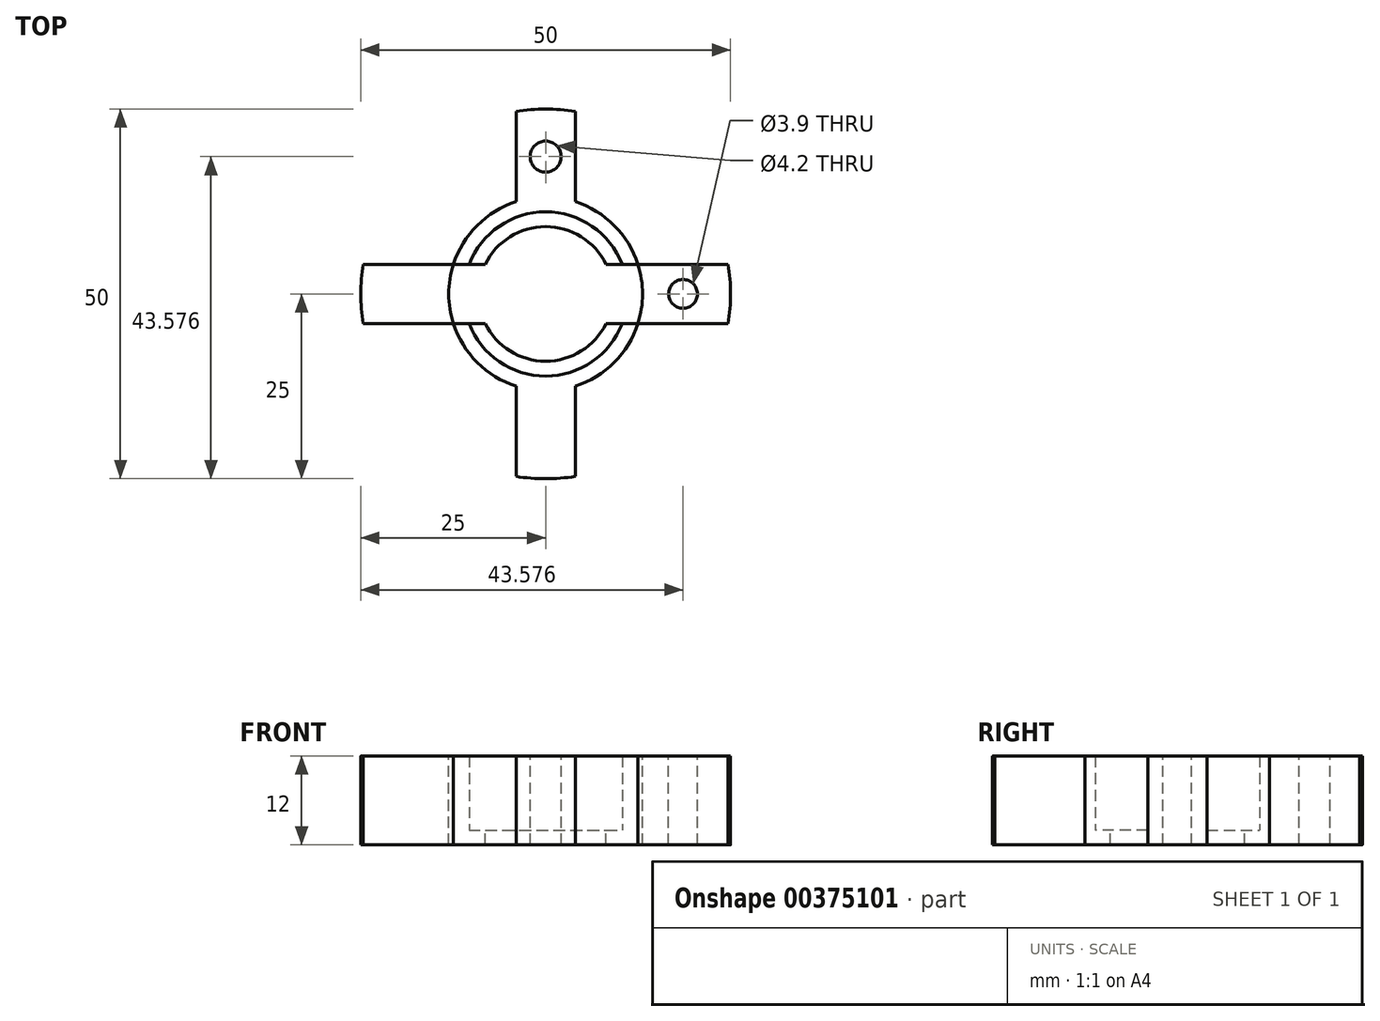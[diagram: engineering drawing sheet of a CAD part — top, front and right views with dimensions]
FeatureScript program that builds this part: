
annotation { "Feature Type Name" : "Feature", "Feature Type Description" : "" }
export const myFeature = defineFeature(function(context is Context, id is Id, definition is map)
    precondition{}
    {
        {
            var Q0;
            Q0=qCreatedBy(makeId("Top.planeOp"),FACE);
            var sketch = newSketch(context, id + "F0", { "sketchPlane" : qUnion([Q0])});
            skCircle(sketch, "E0", {"center": v(0, 0) * mm, "radius": 11.1 * mm});
            skCircle(sketch, "E1.0", {"center": v(0, 0) * mm, "radius": 13.1 * mm});
            skCircle(sketch, "E2.0", {"center": v(0, 0) * mm, "radius": 9.1 * mm});
            skCircle(sketch, "E3", {"center": v(0, 0) * mm, "radius": 25 * mm});
            skLineSegment(sketch, "E4.bottom", {"start": v(-4, -24.68) * mm, "end": v(4, -24.68) * mm});
            skLineSegment(sketch, "E4.top", {"start": v(-4, 24.68) * mm, "end": v(4, 24.68) * mm});
            skLineSegment(sketch, "E4.left", {"start": v(-4, -24.68) * mm, "end": v(-4, 24.68) * mm});
            skLineSegment(sketch, "E4.right", {"start": v(4, -24.68) * mm, "end": v(4, 24.68) * mm});
            skLineSegment(sketch, "E5.bottom", {"start": v(-24.68, -4) * mm, "end": v(24.68, -4) * mm});
            skLineSegment(sketch, "E5.top", {"start": v(-24.68, 4) * mm, "end": v(24.68, 4) * mm});
            skLineSegment(sketch, "E5.left", {"start": v(-24.68, -4) * mm, "end": v(-24.68, 4) * mm});
            skLineSegment(sketch, "E5.right", {"start": v(24.68, -4) * mm, "end": v(24.68, 4) * mm});
            skSolve(sketch);
        }
        {
            var Q0;
            {var subQ5=sQuery(id+"F0.wireOp",EDGE,"E4.top");Q0=makeQuery(id+"F0.imprint","IMPRINT",FACE,{"disambiguationData":[TD([[makeQuery(id+"F0.imprint","IMPRINT",EDGE,{"derivedFrom":subQ5}),-1.0]])]});}
            var Q1;
            {var subQ0=sQuery(id+"F0.wireOp",EDGE,"E4.top");Q1=makeQuery(id+"F0.imprint","IMPRINT",FACE,{"disambiguationData":[TD([[makeQuery(id+"F0.imprint","IMPRINT",EDGE,{"derivedFrom":subQ0}),1.0]])]});}
            var Q2;
            {var subQ0=sQuery(id+"F0.wireOp",EDGE,"E5.right");Q2=makeQuery(id+"F0.imprint","IMPRINT",FACE,{"disambiguationData":[TD([[makeQuery(id+"F0.imprint","IMPRINT",EDGE,{"derivedFrom":subQ0}),-1.0]])]});}
            var Q3;
            {var subQ5=sQuery(id+"F0.wireOp",EDGE,"E5.right");Q3=makeQuery(id+"F0.imprint","IMPRINT",FACE,{"disambiguationData":[TD([[makeQuery(id+"F0.imprint","IMPRINT",EDGE,{"derivedFrom":subQ5}),1.0]])]});}
            var Q4;
            {var subQ0=sQuery(id+"F0.wireOp",EDGE,"E4.bottom");Q4=makeQuery(id+"F0.imprint","IMPRINT",FACE,{"disambiguationData":[TD([[makeQuery(id+"F0.imprint","IMPRINT",EDGE,{"derivedFrom":subQ0}),-1.0]])]});}
            var Q5;
            {var subQ0=sQuery(id+"F0.wireOp",EDGE,"E5.left");Q5=makeQuery(id+"F0.imprint","IMPRINT",FACE,{"disambiguationData":[TD([[makeQuery(id+"F0.imprint","IMPRINT",EDGE,{"derivedFrom":subQ0}),1.0]])]});}
            var Q6;
            {var subQ5=sQuery(id+"F0.wireOp",EDGE,"E5.left");Q6=makeQuery(id+"F0.imprint","IMPRINT",FACE,{"disambiguationData":[TD([[makeQuery(id+"F0.imprint","IMPRINT",EDGE,{"derivedFrom":subQ5}),-1.0]])]});}
            var Q7;
            {var subQ5=sQuery(id+"F0.wireOp",EDGE,"E4.bottom");Q7=makeQuery(id+"F0.imprint","IMPRINT",FACE,{"disambiguationData":[TD([[makeQuery(id+"F0.imprint","IMPRINT",EDGE,{"derivedFrom":subQ5}),1.0]])]});}
            var Q8;
            {var subQ0=sQuery(id+"F0.wireOp",EDGE,"E5.bottom");var subQ1=sQuery(id+"F0.wireOp",EDGE,"E0");var subQ2=makeQuery(id+"F0.imprint","INTERSECT",VERTEX,{"disambiguationData":[OD(0.0)],"derivedFrom":[subQ1,subQ0]});Q8=makeQuery(id+"F0.imprint","IMPRINT",FACE,{"disambiguationData":[TD([[makeQuery(id+"F0.imprint","IMPRINT",EDGE,{"disambiguationData":[TD([[subQ2,-1.0]])],"derivedFrom":subQ1}),-1.0]])]});}
            var Q9;
            {var subQ0=sQuery(id+"F0.wireOp",EDGE,"E5.bottom");var subQ1=sQuery(id+"F0.wireOp",EDGE,"E0");var subQ2=makeQuery(id+"F0.imprint","INTERSECT",VERTEX,{"disambiguationData":[OD(0.0)],"derivedFrom":[subQ1,subQ0]});Q9=makeQuery(id+"F0.imprint","IMPRINT",FACE,{"disambiguationData":[TD([[makeQuery(id+"F0.imprint","IMPRINT",EDGE,{"disambiguationData":[TD([[subQ2,-1.0]])],"derivedFrom":subQ1}),1.0]])]});}
            var Q10;
            {var subQ0=sQuery(id+"F0.wireOp",EDGE,"E5.top");var subQ1=sQuery(id+"F0.wireOp",EDGE,"E0");var subQ2=makeQuery(id+"F0.imprint","INTERSECT",VERTEX,{"disambiguationData":[OD(1.0)],"derivedFrom":[subQ1,subQ0]});Q10=makeQuery(id+"F0.imprint","IMPRINT",FACE,{"disambiguationData":[TD([[makeQuery(id+"F0.imprint","IMPRINT",EDGE,{"disambiguationData":[TD([[subQ2,-1.0]])],"derivedFrom":subQ1}),1.0]])]});}
            var Q11;
            {var subQ0=sQuery(id+"F0.wireOp",EDGE,"E5.top");var subQ1=sQuery(id+"F0.wireOp",EDGE,"E0");var subQ2=makeQuery(id+"F0.imprint","INTERSECT",VERTEX,{"disambiguationData":[OD(1.0)],"derivedFrom":[subQ1,subQ0]});Q11=makeQuery(id+"F0.imprint","IMPRINT",FACE,{"disambiguationData":[TD([[makeQuery(id+"F0.imprint","IMPRINT",EDGE,{"disambiguationData":[TD([[subQ2,-1.0]])],"derivedFrom":subQ1}),-1.0]])]});}
            var Q12;
            {var subQ0=sQuery(id+"F0.wireOp",EDGE,"E4.left");var subQ1=sQuery(id+"F0.wireOp",EDGE,"E0");var subQ2=makeQuery(id+"F0.imprint","INTERSECT",VERTEX,{"disambiguationData":[OD(0.0)],"derivedFrom":[subQ1,subQ0]});Q12=makeQuery(id+"F0.imprint","IMPRINT",FACE,{"disambiguationData":[TD([[makeQuery(id+"F0.imprint","IMPRINT",EDGE,{"disambiguationData":[TD([[subQ2,-1.0]])],"derivedFrom":subQ1}),-1.0]])]});}
            var Q13;
            {var subQ0=sQuery(id+"F0.wireOp",EDGE,"E4.left");var subQ1=sQuery(id+"F0.wireOp",EDGE,"E0");var subQ2=makeQuery(id+"F0.imprint","INTERSECT",VERTEX,{"disambiguationData":[OD(0.0)],"derivedFrom":[subQ1,subQ0]});Q13=makeQuery(id+"F0.imprint","IMPRINT",FACE,{"disambiguationData":[TD([[makeQuery(id+"F0.imprint","IMPRINT",EDGE,{"disambiguationData":[TD([[subQ2,-1.0]])],"derivedFrom":subQ1}),1.0]])]});}
            var Q14;
            {var subQ0=sQuery(id+"F0.wireOp",EDGE,"E4.right");var subQ1=sQuery(id+"F0.wireOp",EDGE,"E0");var subQ2=makeQuery(id+"F0.imprint","INTERSECT",VERTEX,{"disambiguationData":[OD(0.0)],"derivedFrom":[subQ1,subQ0]});Q14=makeQuery(id+"F0.imprint","IMPRINT",FACE,{"disambiguationData":[TD([[makeQuery(id+"F0.imprint","IMPRINT",EDGE,{"disambiguationData":[TD([[subQ2,-1.0]])],"derivedFrom":subQ1}),1.0]])]});}
            var Q15;
            {var subQ0=sQuery(id+"F0.wireOp",EDGE,"E4.right");var subQ1=sQuery(id+"F0.wireOp",EDGE,"E0");var subQ2=makeQuery(id+"F0.imprint","INTERSECT",VERTEX,{"disambiguationData":[OD(0.0)],"derivedFrom":[subQ1,subQ0]});Q15=makeQuery(id+"F0.imprint","IMPRINT",FACE,{"disambiguationData":[TD([[makeQuery(id+"F0.imprint","IMPRINT",EDGE,{"disambiguationData":[TD([[subQ2,-1.0]])],"derivedFrom":subQ1}),-1.0]])]});}
            var Q16;
            {var subQ0=sQuery(id+"F0.wireOp",EDGE,"E4.right");var subQ1=sQuery(id+"F0.wireOp",EDGE,"E0");var subQ2=makeQuery(id+"F0.imprint","INTERSECT",VERTEX,{"disambiguationData":[OD(0.0)],"derivedFrom":[subQ1,subQ0]});Q16=makeQuery(id+"F0.imprint","IMPRINT",FACE,{"disambiguationData":[TD([[makeQuery(id+"F0.imprint","IMPRINT",EDGE,{"disambiguationData":[TD([[subQ2,1.0]])],"derivedFrom":subQ1}),-1.0]])]});}
            var Q17;
            {var subQ0=sQuery(id+"F0.wireOp",EDGE,"E4.right");var subQ1=sQuery(id+"F0.wireOp",EDGE,"E0");var subQ2=makeQuery(id+"F0.imprint","INTERSECT",VERTEX,{"disambiguationData":[OD(0.0)],"derivedFrom":[subQ1,subQ0]});Q17=makeQuery(id+"F0.imprint","IMPRINT",FACE,{"disambiguationData":[TD([[makeQuery(id+"F0.imprint","IMPRINT",EDGE,{"disambiguationData":[TD([[subQ2,1.0]])],"derivedFrom":subQ1}),1.0]])]});}
            var Q18;
            {var subQ0=sQuery(id+"F0.wireOp",EDGE,"E5.top");var subQ1=sQuery(id+"F0.wireOp",EDGE,"E0");var subQ2=makeQuery(id+"F0.imprint","INTERSECT",VERTEX,{"disambiguationData":[OD(0.0)],"derivedFrom":[subQ1,subQ0]});Q18=makeQuery(id+"F0.imprint","IMPRINT",FACE,{"disambiguationData":[TD([[makeQuery(id+"F0.imprint","IMPRINT",EDGE,{"disambiguationData":[TD([[subQ2,1.0]])],"derivedFrom":subQ1}),-1.0]])]});}
            var Q19;
            {var subQ0=sQuery(id+"F0.wireOp",EDGE,"E5.top");var subQ1=sQuery(id+"F0.wireOp",EDGE,"E0");var subQ2=makeQuery(id+"F0.imprint","INTERSECT",VERTEX,{"disambiguationData":[OD(0.0)],"derivedFrom":[subQ1,subQ0]});Q19=makeQuery(id+"F0.imprint","IMPRINT",FACE,{"disambiguationData":[TD([[makeQuery(id+"F0.imprint","IMPRINT",EDGE,{"disambiguationData":[TD([[subQ2,1.0]])],"derivedFrom":subQ1}),1.0]])]});}
            var Q20;
            {var subQ0=sQuery(id+"F0.wireOp",EDGE,"E4.right");var subQ1=sQuery(id+"F0.wireOp",EDGE,"E0");var subQ2=makeQuery(id+"F0.imprint","INTERSECT",VERTEX,{"disambiguationData":[OD(1.0)],"derivedFrom":[subQ1,subQ0]});Q20=makeQuery(id+"F0.imprint","IMPRINT",FACE,{"disambiguationData":[TD([[makeQuery(id+"F0.imprint","IMPRINT",EDGE,{"disambiguationData":[TD([[subQ2,-1.0]])],"derivedFrom":subQ1}),-1.0]])]});}
            var Q21;
            {var subQ0=sQuery(id+"F0.wireOp",EDGE,"E4.right");var subQ1=sQuery(id+"F0.wireOp",EDGE,"E0");var subQ2=makeQuery(id+"F0.imprint","INTERSECT",VERTEX,{"disambiguationData":[OD(1.0)],"derivedFrom":[subQ1,subQ0]});Q21=makeQuery(id+"F0.imprint","IMPRINT",FACE,{"disambiguationData":[TD([[makeQuery(id+"F0.imprint","IMPRINT",EDGE,{"disambiguationData":[TD([[subQ2,-1.0]])],"derivedFrom":subQ1}),1.0]])]});}
            var Q22;
            {var subQ0=sQuery(id+"F0.wireOp",EDGE,"E4.left");var subQ1=sQuery(id+"F0.wireOp",EDGE,"E0");var subQ2=makeQuery(id+"F0.imprint","INTERSECT",VERTEX,{"disambiguationData":[OD(1.0)],"derivedFrom":[subQ1,subQ0]});Q22=makeQuery(id+"F0.imprint","IMPRINT",FACE,{"disambiguationData":[TD([[makeQuery(id+"F0.imprint","IMPRINT",EDGE,{"disambiguationData":[TD([[subQ2,-1.0]])],"derivedFrom":subQ1}),1.0]])]});}
            var Q23;
            {var subQ0=sQuery(id+"F0.wireOp",EDGE,"E4.left");var subQ1=sQuery(id+"F0.wireOp",EDGE,"E0");var subQ2=makeQuery(id+"F0.imprint","INTERSECT",VERTEX,{"disambiguationData":[OD(1.0)],"derivedFrom":[subQ1,subQ0]});Q23=makeQuery(id+"F0.imprint","IMPRINT",FACE,{"disambiguationData":[TD([[makeQuery(id+"F0.imprint","IMPRINT",EDGE,{"disambiguationData":[TD([[subQ2,-1.0]])],"derivedFrom":subQ1}),-1.0]])]});}
            extrude(context, id + "F1", {"entities" : qUnion([Q0, Q1, Q2, Q3, Q4, Q5, Q6, Q7, Q8, Q9, Q10, Q11, Q12, Q13, Q14, Q15, Q16, Q17, Q18, Q19, Q20, Q21, Q22, Q23]), "oppositeDirection" : true, "depth" : 2 * mm});
        }
        {
            var Q0;
            {var subQ0=sQuery(id+"F0.wireOp",EDGE,"E4.right");var subQ1=sQuery(id+"F0.wireOp",EDGE,"E0");var subQ2=makeQuery(id+"F0.imprint","INTERSECT",VERTEX,{"disambiguationData":[OD(0.0)],"derivedFrom":[subQ1,subQ0]});Q0=makeQuery(id+"F0.imprint","IMPRINT",FACE,{"disambiguationData":[TD([[makeQuery(id+"F0.imprint","IMPRINT",EDGE,{"disambiguationData":[TD([[subQ2,-1.0]])],"derivedFrom":subQ1}),-1.0]])]});}
            var Q1;
            {var subQ0=sQuery(id+"F0.wireOp",EDGE,"E4.right");var subQ1=sQuery(id+"F0.wireOp",EDGE,"E0");var subQ2=makeQuery(id+"F0.imprint","INTERSECT",VERTEX,{"disambiguationData":[OD(0.0)],"derivedFrom":[subQ1,subQ0]});Q1=makeQuery(id+"F0.imprint","IMPRINT",FACE,{"disambiguationData":[TD([[makeQuery(id+"F0.imprint","IMPRINT",EDGE,{"disambiguationData":[TD([[subQ2,1.0]])],"derivedFrom":subQ1}),-1.0]])]});}
            var Q2;
            {var subQ5=sQuery(id+"F0.wireOp",EDGE,"E4.top");Q2=makeQuery(id+"F0.imprint","IMPRINT",FACE,{"disambiguationData":[TD([[makeQuery(id+"F0.imprint","IMPRINT",EDGE,{"derivedFrom":subQ5}),-1.0]])]});}
            var Q3;
            {var subQ0=sQuery(id+"F0.wireOp",EDGE,"E4.left");var subQ1=sQuery(id+"F0.wireOp",EDGE,"E0");var subQ2=makeQuery(id+"F0.imprint","INTERSECT",VERTEX,{"disambiguationData":[OD(0.0)],"derivedFrom":[subQ1,subQ0]});Q3=makeQuery(id+"F0.imprint","IMPRINT",FACE,{"disambiguationData":[TD([[makeQuery(id+"F0.imprint","IMPRINT",EDGE,{"disambiguationData":[TD([[subQ2,-1.0]])],"derivedFrom":subQ1}),-1.0]])]});}
            var Q4;
            {var subQ0=sQuery(id+"F0.wireOp",EDGE,"E5.top");var subQ1=sQuery(id+"F0.wireOp",EDGE,"E0");var subQ2=makeQuery(id+"F0.imprint","INTERSECT",VERTEX,{"disambiguationData":[OD(1.0)],"derivedFrom":[subQ1,subQ0]});Q4=makeQuery(id+"F0.imprint","IMPRINT",FACE,{"disambiguationData":[TD([[makeQuery(id+"F0.imprint","IMPRINT",EDGE,{"disambiguationData":[TD([[subQ2,-1.0]])],"derivedFrom":subQ1}),-1.0]])]});}
            var Q5;
            {var subQ5=sQuery(id+"F0.wireOp",EDGE,"E5.left");Q5=makeQuery(id+"F0.imprint","IMPRINT",FACE,{"disambiguationData":[TD([[makeQuery(id+"F0.imprint","IMPRINT",EDGE,{"derivedFrom":subQ5}),-1.0]])]});}
            var Q6;
            {var subQ0=sQuery(id+"F0.wireOp",EDGE,"E5.bottom");var subQ1=sQuery(id+"F0.wireOp",EDGE,"E0");var subQ2=makeQuery(id+"F0.imprint","INTERSECT",VERTEX,{"disambiguationData":[OD(0.0)],"derivedFrom":[subQ1,subQ0]});Q6=makeQuery(id+"F0.imprint","IMPRINT",FACE,{"disambiguationData":[TD([[makeQuery(id+"F0.imprint","IMPRINT",EDGE,{"disambiguationData":[TD([[subQ2,-1.0]])],"derivedFrom":subQ1}),-1.0]])]});}
            var Q7;
            {var subQ0=sQuery(id+"F0.wireOp",EDGE,"E4.left");var subQ1=sQuery(id+"F0.wireOp",EDGE,"E0");var subQ2=makeQuery(id+"F0.imprint","INTERSECT",VERTEX,{"disambiguationData":[OD(1.0)],"derivedFrom":[subQ1,subQ0]});Q7=makeQuery(id+"F0.imprint","IMPRINT",FACE,{"disambiguationData":[TD([[makeQuery(id+"F0.imprint","IMPRINT",EDGE,{"disambiguationData":[TD([[subQ2,-1.0]])],"derivedFrom":subQ1}),-1.0]])]});}
            var Q8;
            {var subQ5=sQuery(id+"F0.wireOp",EDGE,"E4.bottom");Q8=makeQuery(id+"F0.imprint","IMPRINT",FACE,{"disambiguationData":[TD([[makeQuery(id+"F0.imprint","IMPRINT",EDGE,{"derivedFrom":subQ5}),1.0]])]});}
            var Q9;
            {var subQ0=sQuery(id+"F0.wireOp",EDGE,"E4.right");var subQ1=sQuery(id+"F0.wireOp",EDGE,"E0");var subQ2=makeQuery(id+"F0.imprint","INTERSECT",VERTEX,{"disambiguationData":[OD(1.0)],"derivedFrom":[subQ1,subQ0]});Q9=makeQuery(id+"F0.imprint","IMPRINT",FACE,{"disambiguationData":[TD([[makeQuery(id+"F0.imprint","IMPRINT",EDGE,{"disambiguationData":[TD([[subQ2,-1.0]])],"derivedFrom":subQ1}),-1.0]])]});}
            var Q10;
            {var subQ0=sQuery(id+"F0.wireOp",EDGE,"E5.top");var subQ1=sQuery(id+"F0.wireOp",EDGE,"E0");var subQ2=makeQuery(id+"F0.imprint","INTERSECT",VERTEX,{"disambiguationData":[OD(0.0)],"derivedFrom":[subQ1,subQ0]});Q10=makeQuery(id+"F0.imprint","IMPRINT",FACE,{"disambiguationData":[TD([[makeQuery(id+"F0.imprint","IMPRINT",EDGE,{"disambiguationData":[TD([[subQ2,1.0]])],"derivedFrom":subQ1}),-1.0]])]});}
            var Q11;
            {var subQ5=sQuery(id+"F0.wireOp",EDGE,"E5.right");Q11=makeQuery(id+"F0.imprint","IMPRINT",FACE,{"disambiguationData":[TD([[makeQuery(id+"F0.imprint","IMPRINT",EDGE,{"derivedFrom":subQ5}),1.0]])]});}
            var Q12;
            {var subQ0=sQuery(id+"F0.wireOp",EDGE,"E5.right");Q12=makeQuery(id+"F0.imprint","IMPRINT",FACE,{"disambiguationData":[TD([[makeQuery(id+"F0.imprint","IMPRINT",EDGE,{"derivedFrom":subQ0}),-1.0]])]});}
            var Q13;
            {var subQ0=sQuery(id+"F0.wireOp",EDGE,"E4.bottom");Q13=makeQuery(id+"F0.imprint","IMPRINT",FACE,{"disambiguationData":[TD([[makeQuery(id+"F0.imprint","IMPRINT",EDGE,{"derivedFrom":subQ0}),-1.0]])]});}
            var Q14;
            {var subQ0=sQuery(id+"F0.wireOp",EDGE,"E5.left");Q14=makeQuery(id+"F0.imprint","IMPRINT",FACE,{"disambiguationData":[TD([[makeQuery(id+"F0.imprint","IMPRINT",EDGE,{"derivedFrom":subQ0}),1.0]])]});}
            var Q15;
            {var subQ0=sQuery(id+"F0.wireOp",EDGE,"E4.top");Q15=makeQuery(id+"F0.imprint","IMPRINT",FACE,{"disambiguationData":[TD([[makeQuery(id+"F0.imprint","IMPRINT",EDGE,{"derivedFrom":subQ0}),1.0]])]});}
            extrude(context, id + "F2", {"entities" : qUnion([Q0, Q1, Q2, Q3, Q4, Q5, Q6, Q7, Q8, Q9, Q10, Q11, Q12, Q13, Q14, Q15]), "operationType" : NewBodyOperationType.ADD, "depth" : (6 + 2 + 2) * mm});
        }
        {
            var Q0;
            Q0=makeQuery(id+"F2.opExtrude","CAP_FACE",FACE,{"disambiguationData":[OSD([sQuery(id+"F0.wireOp",EDGE,"E0"),sQuery(id+"F0.wireOp",EDGE,"E1.0"),sQuery(id+"F0.wireOp",EDGE,"E3"),sQuery(id+"F0.wireOp",EDGE,"E4.left"),sQuery(id+"F0.wireOp",EDGE,"E4.right"),sQuery(id+"F0.wireOp",EDGE,"E5.bottom"),sQuery(id+"F0.wireOp",EDGE,"E5.top")])],"isStart":false});
            var sketch = newSketch(context, id + "F3", { "sketchPlane" : qUnion([Q0])});
            skCircle(sketch, "E6", {"center": v(18.58, 0) * mm, "radius": 1.95 * mm});
            skCircle(sketch, "E7", {"center": v(0, -18.58) * mm, "radius": 2.1 * mm});
            skCircle(sketch, "E8.MirrorC", {"center": v(-18.58, 0) * mm, "radius": 1.95 * mm});
            skCircle(sketch, "E9.MirrorC", {"center": v(0, 18.58) * mm, "radius": 2.1 * mm});
            skLineSegment(sketch, "E10", {"start": v(18.58, 4) * mm, "end": v(18.58, -4) * mm, "construction": true});
            skLineSegment(sketch, "E11", {"start": v(4, -18.58) * mm, "end": v(-4, -18.58) * mm, "construction": true});
            skSolve(sketch);
        }
        {
            var Q0;
            Q0=makeQuery(id+"F3.imprint","IMPRINT",FACE,{"disambiguationData":[TD([[makeQuery(id+"F3.imprint","IMPRINT",EDGE,{"derivedFrom":sQuery(id+"F3.wireOp",EDGE,"E6")}),1.0]])]});
            var Q1;
            Q1=makeQuery(id+"F3.imprint","IMPRINT",FACE,{"disambiguationData":[TD([[makeQuery(id+"F3.imprint","IMPRINT",EDGE,{"derivedFrom":sQuery(id+"F3.wireOp",EDGE,"E9.MirrorC")}),1.0]])]});
            var Q2;
            Q2=makeQuery(id+"F3.imprint","IMPRINT",FACE,{"disambiguationData":[TD([[makeQuery(id+"F3.imprint","IMPRINT",EDGE,{"derivedFrom":sQuery(id+"F3.wireOp",EDGE,"E7")}),-1.0]])]});
            var Q3;
            Q3=makeQuery(id+"F3.imprint","IMPRINT",FACE,{"disambiguationData":[TD([[makeQuery(id+"F3.imprint","IMPRINT",EDGE,{"derivedFrom":sQuery(id+"F3.wireOp",EDGE,"E8.MirrorC")}),-1.0]])]});
            extrude(context, id + "F4", {"entities" : qUnion([Q0, Q1, Q2, Q3]), "operationType" : NewBodyOperationType.REMOVE, "endBound" : BoundingType.THROUGH_ALL, "oppositeDirection" : true, "depth" : 25 * mm});
        }
    });
